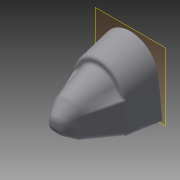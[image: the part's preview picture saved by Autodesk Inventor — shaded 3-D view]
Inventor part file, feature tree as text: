
AUTODESK INVENTOR PART (.ipt)
format: ipt  version: 2015 (Build 190159000, 159)  size: 1,775,616 bytes
history: native  units: in
note: dims shown in document units (in); Inventor stores cm internally (conversion verified against a paired STEP export)
features: sketch x29, plane x14, loft x11, extrude x9, fillet x6, other x3, projected_geometry x3, mirror x2, chamfer x2
ambient origin geometry x8: Origin, YZ Plane, XZ Plane, XY Plane, X Axis, Y Axis, Z Axis, Center Point
bodies: Solid1 (feature_tree)
feature tree (79):
  extrude  "Extrusion1"  TaperAngle=0.0deg  [1 undecoded]
  plane  "Work Plane1"
  plane  "Work Plane2"
  plane  "Work Plane3"
  loft  "Loft1"
  loft  "Loft2"
  fillet  "Fillet1"  Radius=240.6614in
  loft  "Loft4"
  fillet  "Fillet2"  Radius=125.0in
  extrude  "Extrusion2"  TaperAngle=0.0deg  [1 undecoded]
  extrude  "Extrusion3"  Depth=100.0in
  fillet  "Fillet3"  [1 undecoded]
  plane  "Work Plane4"
  mirror  "Mirror1"
  plane  "Work Plane5"
  sketch  "Sketch12"  dims[d36=0.0in d37=90.0deg d38=125.0in]
  loft  "Loft5"
  chamfer  "Chamfer1"  Angle=90.0deg  [1 undecoded]
  chamfer  "Chamfer2"  Angle=90.0deg  [1 undecoded]
  sketch  "Sketch15"  dims[d39=15.0in]
  plane  "Work Plane6"
  plane  "Work Plane7"
  loft  "Loft8"
  mirror  "Mirror2"
  extrude  "Extrusion5"  Depth=125.0in
  extrude  "Extrusion6"  TaperAngle=0.0deg  [1 undecoded]
  plane  "Work Plane8"
  sketch  "Sketch20"  dims[d51=10.0in]
  plane  "Work Plane10"
  loft  "Loft9"
  fillet  "Fillet4"  Radius=84.0in
  extrude  "Extrusion7"  Depth=0.6803in
  fillet  "Fillet5"  Radius=48.0in
  fillet  "Fillet6"  Radius=6500.0in
  sketch  "Sketch23"  dims[d55=0.0in]
  plane  "Work Plane11"
  sketch  "Sketch24"  dims[d56=0.0in]
  loft  "Loft10"
  loft  "Loft11"
  sketch  "Sketch27"  dims[d64=60.0in d70=125.0in]
  plane  "Work Plane12"
  loft  "Loft12"
  loft  "Loft13"
  loft  "Loft14"
  sketch  "Sketch31"  dims[d89=6500.0in d90=7700.0in]
  plane  "Work Plane13"
  sketch  "Sketch32"  dims[d91=10.0in d92=345.0in d93=0.0in]
  sketch  "Sketch33"  dims[d94=10.0in d95=125.0in]
  plane  "Work Plane14"
  extrude  "Extrusion8"  Depth=245.0in
  sketch  "Sketch35"  dims[d98=10.0in d99=0.0in]
  plane  "Work Plane15"
  extrude  "Extrusion9"  Depth=15.0in
  extrude  "Extrusion10"  Depth=0.0618in
  sketch  "Sketch1"  dims[d5=250.0in d12=0.0in]
  sketch  "Sketch2"  dims[d13=75.0in d15=110.0in]
  other  "Edges1"
  sketch  "Sketch3"  dims[d21=98.0in d24=110.0in d25=240.6614in]
  sketch  "Sketch6"  dims[d26=730.0in d27=0.0in d28=300.0in d29=125.0in]
  sketch  "Sketch7"  dims[d30=250.0in d31=0.0in]
  other  "Edges3"
  sketch  "Sketch8"  dims[d32=125.0in d33=100.0in d34=0.0in d35=90.0deg]
  other  "Edges4"
  sketch  "Sketch17"  dims[d40=20.0in]
  sketch  "Sketch18"  dims[d41=10.0in]
  sketch  "Sketch19"  dims[d50=15.0in]
  projected_geometry  "Projected Loop7"
  sketch  "Sketch21"  dims[d52=75.0in]
  sketch  "Sketch22"  dims[d54=125.0in]
  sketch  "Sketch25"  dims[d57=0.0in d58=0.0in d59=90.0deg d60=0.0in d61=90.0deg]
  sketch  "Sketch26"  dims[d62=10.65in d63=50.0in]
  sketch  "Sketch28"  dims[d71=50.0in d72=0.0in d73=90.0deg]
  sketch  "Sketch29"  dims[d74=0.0in d75=90.0deg d76=40.0in d79=84.0in]
  sketch  "Sketch30"  dims[d80=0.0in d82=0.6803in d83=48.0in d84=0.0in d85=6500.0in]
  sketch  "Sketch34"  dims[d96=200.0in d97=0.0in]
  projected_geometry  "Projected Loop8"
  projected_geometry  "Projected Loop9"
  sketch  "Sketch36"  dims[d100=0.0in d101=245.0in]
  sketch  "Sketch37"  dims[d102=90.0in d105=15.0in d106=0.0618in d107=45.0deg d108=345.0in d109=0.0in d110=90.0deg d111=0.0in d112=90.0deg d113=5.2in d114=0.125in d115=45.0deg d116=5.2in d117=0.125in d118=45.0deg d119=-200.0in d126=100.0in d127=25.0in d133=-205.0in d134=50.0in d135=60.0in d137=0.0in d138=90.0deg d139=0.0in d140=90.0deg d141=160.0in d142=100.0in d143=0.6528in d144=0.0in d145=0.0in d146=9000.0in d147=0.0in d148=15.0in d149=25.0in d150=0.0in d151=30.0in d152=0.0in d153=-20.0in d154=30.0in d155=10.0in d156=1.2162in d157=1.2162in d158=195.0in d160=225.0in d166=30.0in d167=225.0in d168=20.0in d169=30.0in d170=20.0in d171=80.0in d172=0.0in d173=90.0deg d174=0.0in d175=90.0deg d176=7.0in d177=0.1374in d178=200.0in d179=0.0in d180=9.475in d184=150.0in d185=150.0in d186=9.475in d187=40.0in d188=80.0in d189=65.0in d190=60.0in d191=20.0in d192=125.0in d193=0.0in d194=13.0in d195=32.0in d196=55.0in d197=55.0in d198=55.0in d199=80.0in d200=95.0in d201=95.0in d202=40.0in d203=0.0in d204=90.0deg d205=0.0in d206=90.0deg d207=0.0in d208=90.0deg d209=0.0in d210=90.0deg d211=25.0in d212=90.0in d213=8.0in d214=0.0in d215=90.0deg d216=0.0in d217=90.0deg d218=105.0in d219=5.0in d220=5.0in d221=0.0in d222=90.0deg d223=0.0in d224=90.0deg d225=105.0in d226=5.0in d227=5.0in d228=0.0in d229=90.0deg d230=0.0in d231=90.0deg d232=-20.0in d233=90.0deg d234=95.0in d235=0.0in d236=90.0deg d237=105.0in d238=0.0in d239=9000.0in d240=0.0in]
note: 6 required parameter values undecoded (feature->parameter linkage not recoverable at this tier; creation-order binding heuristic only, values carry confidence <= 0.55)
